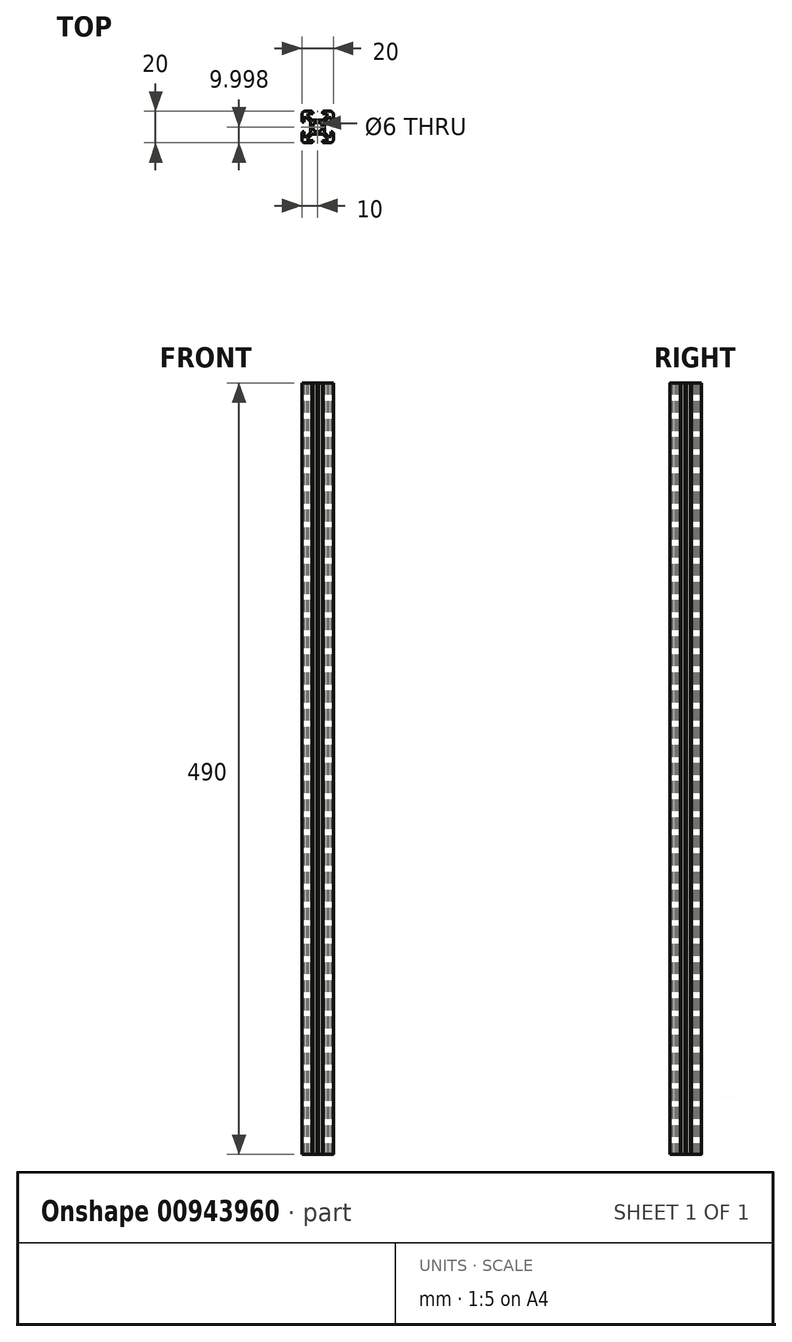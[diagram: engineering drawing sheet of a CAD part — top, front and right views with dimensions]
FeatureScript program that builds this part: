
annotation { "Feature Type Name" : "Feature", "Feature Type Description" : "" }
export const myFeature = defineFeature(function(context is Context, id is Id, definition is map)
    precondition{}
    {
        {
            var Q0;
            Q0=qCreatedBy(makeId("Top.planeOp"),FACE);
            var sketch = newSketch(context, id + "F0", { "sketchPlane" : qUnion([Q0])});
            skLineSegment(sketch, "E0.bottom", {"start": v(-8, -10) * mm, "end": v(8, -10) * mm});
            skLineSegment(sketch, "E0.top", {"start": v(-8, 10) * mm, "end": v(8, 10) * mm});
            skLineSegment(sketch, "E0.left", {"start": v(-10, -8) * mm, "end": v(-10, 8) * mm});
            skLineSegment(sketch, "E0.right", {"start": v(10, -8) * mm, "end": v(10, 8) * mm});
            skPoint(sketch, "E1.visualSharp", {"position": v(10, 10) * mm});
            skArc(sketch, "E1.filletArc", {"start": v(10, 8) * mm, "mid": v(9.41, 9.42) * mm, "end": v(8, 10) * mm});
            skPoint(sketch, "E2.visualSharp", {"position": v(-10, 10) * mm});
            skArc(sketch, "E2.filletArc", {"start": v(-8, 10) * mm, "mid": v(-9.41, 9.42) * mm, "end": v(-10, 8) * mm});
            skPoint(sketch, "E3.visualSharp", {"position": v(-10, -10) * mm});
            skArc(sketch, "E3.filletArc", {"start": v(-10, -8) * mm, "mid": v(-9.41, -9.4) * mm, "end": v(-8, -10) * mm});
            skPoint(sketch, "E4.visualSharp", {"position": v(10, -10) * mm});
            skArc(sketch, "E4.filletArc", {"start": v(8, -10) * mm, "mid": v(9.41, -9.4) * mm, "end": v(10, -8) * mm});
            skLineSegment(sketch, "E5", {"start": v(-10, -10) * mm, "end": v(10, 10) * mm, "construction": true});
            skLineSegment(sketch, "E6", {"start": v(-10, 10) * mm, "end": v(10, -10) * mm, "construction": true});
            skCircle(sketch, "E7", {"center": v(0, 0) * mm, "radius": 3 * mm});
            skCircle(sketch, "E8", {"center": v(0, 0) * mm, "radius": 2.75 * mm});
            skLineSegment(sketch, "E9.bottom", {"start": v(-2.45, -1.73) * mm, "end": v(-1.74, -2.44) * mm});
            skLineSegment(sketch, "E9.top", {"start": v(1.74, 2.45) * mm, "end": v(2.45, 1.75) * mm});
            skLineSegment(sketch, "E9.left", {"start": v(-2.45, -1.73) * mm, "end": v(1.74, 2.45) * mm});
            skLineSegment(sketch, "E9.right", {"start": v(-1.74, -2.44) * mm, "end": v(2.45, 1.75) * mm});
            skLineSegment(sketch, "E10.bottom", {"start": v(-2.45, 1.75) * mm, "end": v(-1.74, 2.45) * mm});
            skLineSegment(sketch, "E10.top", {"start": v(1.74, -2.44) * mm, "end": v(2.45, -1.73) * mm});
            skLineSegment(sketch, "E10.left", {"start": v(-2.45, 1.75) * mm, "end": v(1.74, -2.44) * mm});
            skLineSegment(sketch, "E10.right", {"start": v(-1.74, 2.45) * mm, "end": v(2.45, -1.73) * mm});
            skLineSegment(sketch, "E11", {"start": v(-3.5, 10) * mm, "end": v(-3.5, 9.5) * mm});
            skLineSegment(sketch, "E12", {"start": v(-3.5, 9.5) * mm, "end": v(-3, 9.5) * mm});
            skLineSegment(sketch, "E13", {"start": v(-3, 9.5) * mm, "end": v(-3, 8.5) * mm});
            skLineSegment(sketch, "E14", {"start": v(-3, 8.5) * mm, "end": v(-6, 8.5) * mm});
            skLineSegment(sketch, "E15", {"start": v(-6, 8.5) * mm, "end": v(-6, 7) * mm});
            skLineSegment(sketch, "E16", {"start": v(-3.5, 4.5) * mm, "end": v(-6, 7) * mm});
            skLineSegment(sketch, "E17", {"start": v(-3.5, 4.5) * mm, "end": v(3.5, 4.5) * mm});
            skLineSegment(sketch, "E18", {"start": v(3.5, 4.5) * mm, "end": v(6, 7) * mm});
            skLineSegment(sketch, "E19", {"start": v(6, 7) * mm, "end": v(6, 8.5) * mm});
            skLineSegment(sketch, "E20", {"start": v(6, 8.5) * mm, "end": v(3, 8.5) * mm});
            skLineSegment(sketch, "E21", {"start": v(3, 8.5) * mm, "end": v(3, 9.5) * mm});
            skLineSegment(sketch, "E22", {"start": v(3, 9.5) * mm, "end": v(3.5, 9.5) * mm});
            skLineSegment(sketch, "E23", {"start": v(3.5, 9.5) * mm, "end": v(3.5, 10) * mm});
            skLineSegment(sketch, "E24", {"start": v(0, 10) * mm, "end": v(0, -11.4) * mm, "construction": true});
            skLineSegment(sketch, "E25.1.0", {"start": v(-8.5, -6) * mm, "end": v(-7, -6) * mm});
            skLineSegment(sketch, "E25.1.1", {"start": v(-8.5, -3) * mm, "end": v(-8.5, -6) * mm});
            skLineSegment(sketch, "E25.1.2", {"start": v(-9.5, -3) * mm, "end": v(-8.5, -3) * mm});
            skLineSegment(sketch, "E25.1.3", {"start": v(-9.5, -3.5) * mm, "end": v(-9.5, -3) * mm});
            skLineSegment(sketch, "E25.1.4", {"start": v(-10, -3.5) * mm, "end": v(-9.5, -3.5) * mm});
            skLineSegment(sketch, "E25.1.5", {"start": v(-4.5, -3.5) * mm, "end": v(-7, -6) * mm});
            skLineSegment(sketch, "E25.1.6", {"start": v(-4.5, -3.5) * mm, "end": v(-4.5, 3.5) * mm});
            skLineSegment(sketch, "E25.1.7", {"start": v(-4.5, 3.5) * mm, "end": v(-7, 6) * mm});
            skLineSegment(sketch, "E25.1.8", {"start": v(-7, 6) * mm, "end": v(-8.5, 6) * mm});
            skLineSegment(sketch, "E25.1.9", {"start": v(-8.5, 6) * mm, "end": v(-8.5, 3) * mm});
            skLineSegment(sketch, "E25.1.10", {"start": v(-8.5, 3) * mm, "end": v(-9.5, 3) * mm});
            skLineSegment(sketch, "E25.1.11", {"start": v(-9.5, 3) * mm, "end": v(-9.5, 3.5) * mm});
            skLineSegment(sketch, "E25.1.12", {"start": v(-9.5, 3.5) * mm, "end": v(-10, 3.5) * mm});
            skLineSegment(sketch, "E25.2.0", {"start": v(6, -8.5) * mm, "end": v(6, -7) * mm});
            skLineSegment(sketch, "E25.2.1", {"start": v(3, -8.5) * mm, "end": v(6, -8.5) * mm});
            skLineSegment(sketch, "E25.2.2", {"start": v(3, -9.5) * mm, "end": v(3, -8.5) * mm});
            skLineSegment(sketch, "E25.2.3", {"start": v(3.5, -9.5) * mm, "end": v(3, -9.5) * mm});
            skLineSegment(sketch, "E25.2.4", {"start": v(3.5, -10) * mm, "end": v(3.5, -9.5) * mm});
            skLineSegment(sketch, "E25.2.5", {"start": v(3.5, -4.5) * mm, "end": v(6, -7) * mm});
            skLineSegment(sketch, "E25.2.6", {"start": v(3.5, -4.5) * mm, "end": v(-3.5, -4.5) * mm});
            skLineSegment(sketch, "E25.2.7", {"start": v(-3.5, -4.5) * mm, "end": v(-6, -7) * mm});
            skLineSegment(sketch, "E25.2.8", {"start": v(-6, -7) * mm, "end": v(-6, -8.5) * mm});
            skLineSegment(sketch, "E25.2.9", {"start": v(-6, -8.5) * mm, "end": v(-3, -8.5) * mm});
            skLineSegment(sketch, "E25.2.10", {"start": v(-3, -8.5) * mm, "end": v(-3, -9.5) * mm});
            skLineSegment(sketch, "E25.2.11", {"start": v(-3, -9.5) * mm, "end": v(-3.5, -9.5) * mm});
            skLineSegment(sketch, "E25.2.12", {"start": v(-3.5, -9.5) * mm, "end": v(-3.5, -10) * mm});
            skLineSegment(sketch, "E25.3.0", {"start": v(8.5, 6) * mm, "end": v(7, 6) * mm});
            skLineSegment(sketch, "E25.3.1", {"start": v(8.5, 3) * mm, "end": v(8.5, 6) * mm});
            skLineSegment(sketch, "E25.3.2", {"start": v(9.5, 3) * mm, "end": v(8.5, 3) * mm});
            skLineSegment(sketch, "E25.3.3", {"start": v(9.5, 3.5) * mm, "end": v(9.5, 3) * mm});
            skLineSegment(sketch, "E25.3.4", {"start": v(10, 3.5) * mm, "end": v(9.5, 3.5) * mm});
            skLineSegment(sketch, "E25.3.5", {"start": v(4.5, 3.5) * mm, "end": v(7, 6) * mm});
            skLineSegment(sketch, "E25.3.6", {"start": v(4.5, 3.5) * mm, "end": v(4.5, -3.5) * mm});
            skLineSegment(sketch, "E25.3.7", {"start": v(4.5, -3.5) * mm, "end": v(7, -6) * mm});
            skLineSegment(sketch, "E25.3.8", {"start": v(7, -6) * mm, "end": v(8.5, -6) * mm});
            skLineSegment(sketch, "E25.3.9", {"start": v(8.5, -6) * mm, "end": v(8.5, -3) * mm});
            skLineSegment(sketch, "E25.3.10", {"start": v(8.5, -3) * mm, "end": v(9.5, -3) * mm});
            skLineSegment(sketch, "E25.3.11", {"start": v(9.5, -3) * mm, "end": v(9.5, -3.5) * mm});
            skLineSegment(sketch, "E25.3.12", {"start": v(9.5, -3.5) * mm, "end": v(10, -3.5) * mm});
            skLineSegment(sketch, "E26", {"start": v(-0.5, 4.5) * mm, "end": v(0, 4) * mm});
            skLineSegment(sketch, "E27", {"start": v(0, 4) * mm, "end": v(0.5, 4.5) * mm});
            skLineSegment(sketch, "E28.1.0", {"start": v(-4, 0) * mm, "end": v(-4.5, 0.5) * mm});
            skLineSegment(sketch, "E28.1.1", {"start": v(-4.5, -0.5) * mm, "end": v(-4, 0) * mm});
            skLineSegment(sketch, "E28.2.0", {"start": v(0, -4) * mm, "end": v(-0.5, -4.5) * mm});
            skLineSegment(sketch, "E28.2.1", {"start": v(0.5, -4.5) * mm, "end": v(0, -4) * mm});
            skLineSegment(sketch, "E28.3.0", {"start": v(4, 0) * mm, "end": v(4.5, -0.5) * mm});
            skLineSegment(sketch, "E28.3.1", {"start": v(4.5, 0.5) * mm, "end": v(4, 0) * mm});
            skSolve(sketch);
        }
        {
            var Q0;
            {var subQ6=sQuery(id+"F0.wireOp",EDGE,"E1.filletArc");Q0=makeQuery(id+"F0.imprint","IMPRINT",FACE,{"disambiguationData":[TD([[makeQuery(id+"F0.imprint","IMPRINT",EDGE,{"derivedFrom":subQ6}),1.0]])]});}
            extrude(context, id + "F1", {"entities" : qUnion([Q0]), "flatOperationType" : FlatOperationType.REMOVE, "depth" : 490 * mm, "offsetDistance" : 25.4 * mm, "domain" : OperationDomain.MODEL});
        }
    });
